# Revit family: 820-00-024 DN25-40
name_source: partatom
category: Pipe Accessories
units: mm (PartAtom-declared; Revit-internal decimal feet)

## family parameters
Always vertical = Yes
Cut with Voids When Loaded = No
Part Type = Valve - Breaks Into
Round Connector Dimension = Use Diameter
Shared = No
Work Plane-Based = No

## types (3) — shared parameters
1 = 1 mm  [stored 0.00328084 ft]
90 = 90 mm  [stored 0.295276 ft]
Actuator_Dia = 65 mm  [stored 0.213255 ft]
Body_wallthickness = 10 mm  [stored 0.0328084 ft]
DN25_PN10/16 = 820-0025-00-521L0160002
DN32_PN10/16 = 820-0032-00-521L0160002
DN40_PN10/16 = 820-0040-00-521L0160002
Description_ = AVK CENTRIC BUTTERFLY VALVE WAFER TYPE, PN10/16
F = 8 mm  [stored 0.0262467 ft]
F2 = 12 mm  [stored 0.0393701 ft]
FL_T = 5 mm  [stored 0.0164042 ft]
Search_table = 820-00-024 DN25-40
URL product pages = https://www.avkvalves.com
fillet = 20 mm  [stored 0.0656168 ft]
zero-valued in all types: Default Elevation

## per-type parameters (varying)
| type | Bore | DN | EPDM | EPDM_R | FL_R | Flange_thickness | H2 | Hole_dia | ID | L | L-2 | L2 | LUG_T | L_ref | L_ref_2 | L_ref_3 | Lug_D | PCD | W2_ref | disk |
| DN25_PN10/16 | 13 mm  [stored 0.0426509 ft] | 25 mm  [stored 0.082021 ft] | 12 mm  [stored 0.0393701 ft] | 23 mm  [stored 0.0754593 ft] | 23 mm  [stored 0.0754593 ft] | 6 mm  [stored 0.019685 ft] | 51 mm  [stored 0.167323 ft] | 14 mm  [stored 0.0459318 ft] | 13 mm  [stored 0.0426509 ft] | 30 mm  [stored 0.0984252 ft] | 28 mm  [stored 0.0918635 ft] | 51 mm  [stored 0.167323 ft] | 11 mm  [stored 0.0360892 ft] | 16 mm  [stored 0.0524934 ft] | 32 mm  [stored 0.104987 ft] | 13 mm  [stored 0.0426509 ft] | 10 mm  [stored 0.0328084 ft] | 43 mm  [stored 0.141076 ft] | 110 mm  [stored 0.360892 ft] | 8 mm  [stored 0.0262467 ft] |
| DN32_PN10/16 | 16 mm  [stored 0.0524934 ft] | 32 mm  [stored 0.104987 ft] | 15 mm  [stored 0.0492126 ft] | 26 mm | 26 mm | 6 mm  [stored 0.019685 ft] | 51 mm  [stored 0.167323 ft] | 19 mm  [stored 0.062336 ft] | 16 mm  [stored 0.0524934 ft] | 30 mm  [stored 0.0984252 ft] | 28 mm  [stored 0.0918635 ft] | 51 mm  [stored 0.167323 ft] | 11 mm  [stored 0.0360892 ft] | 16 mm  [stored 0.0524934 ft] | 32 mm  [stored 0.104987 ft] | 13 mm  [stored 0.0426509 ft] | 13 mm  [stored 0.0426509 ft] | 50 mm  [stored 0.164042 ft] | 110 mm  [stored 0.360892 ft] | 8 mm  [stored 0.0262467 ft] |
| DN40_PN10/16 | 20 mm  [stored 0.0656168 ft] | 40 mm  [stored 0.131234 ft] | 19 mm  [stored 0.062336 ft] | 30 mm  [stored 0.0984252 ft] | 30 mm  [stored 0.0984252 ft] | 7 mm  [stored 0.0229659 ft] | 55 mm  [stored 0.180446 ft] | 19 mm  [stored 0.062336 ft] | 20 mm  [stored 0.0656168 ft] | 33 mm  [stored 0.108268 ft] | 31 mm  [stored 0.101706 ft] | 54 mm  [stored 0.177165 ft] | 12 mm  [stored 0.0393701 ft] | 17 mm  [stored 0.0557743 ft] | 34 mm | 14 mm  [stored 0.0459318 ft] | 13 mm  [stored 0.0426509 ft] | 55 mm  [stored 0.180446 ft] | 130 mm  [stored 0.426509 ft] | 9 mm  [stored 0.0295276 ft] |

note: [stored X ft] marks values corroborated as IEEE doubles in the binary element streams (Revit-internal decimal feet)

## geometry (parser evidence)
native form markers: Sweep x4
no freeform markers — native parametric forms only
